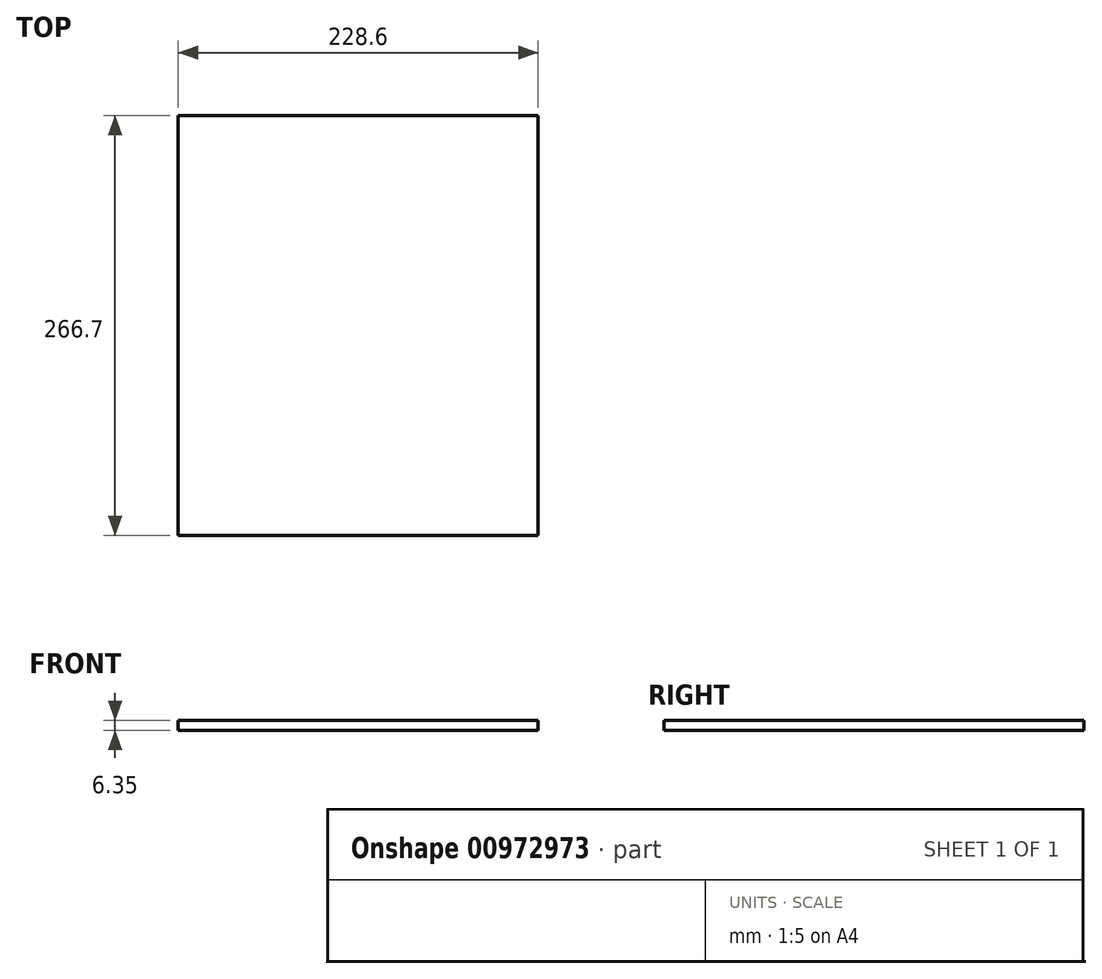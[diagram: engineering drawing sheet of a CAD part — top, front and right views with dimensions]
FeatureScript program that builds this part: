
annotation { "Feature Type Name" : "Feature", "Feature Type Description" : "" }
export const myFeature = defineFeature(function(context is Context, id is Id, definition is map)
    precondition{}
    {
        {
            var Q0;
            Q0=qCreatedBy(makeId("Top.planeOp"),FACE);
            var sketch = newSketch(context, id + "F0", { "sketchPlane" : qUnion([Q0])});
            skLineSegment(sketch, "E0.bottom", {"start": v(-114.3, 133.35) * mm, "end": v(114.3, 133.35) * mm});
            skLineSegment(sketch, "E0.top", {"start": v(-114.3, -133.35) * mm, "end": v(114.3, -133.35) * mm});
            skLineSegment(sketch, "E0.left", {"start": v(-114.3, 133.35) * mm, "end": v(-114.3, -133.35) * mm});
            skLineSegment(sketch, "E0.right", {"start": v(114.3, 133.35) * mm, "end": v(114.3, -133.35) * mm});
            skPoint(sketch, "E0.middle", {"position": v(0, 0) * mm});
            skSolve(sketch);
        }
        {
            var Q0;
            Q0=makeQuery(id+"F0.imprint","IMPRINT",FACE,{"disambiguationData":[TD([[makeQuery(id+"F0.imprint","IMPRINT",EDGE,{"derivedFrom":sQuery(id+"F0.wireOp",EDGE,"E0.bottom")}),-1.0]])]});
            extrude(context, id + "F1", {"entities" : qUnion([Q0]), "depth" : 6.35 * mm, "offsetDistance" : 25.4 * mm});
        }
    });
